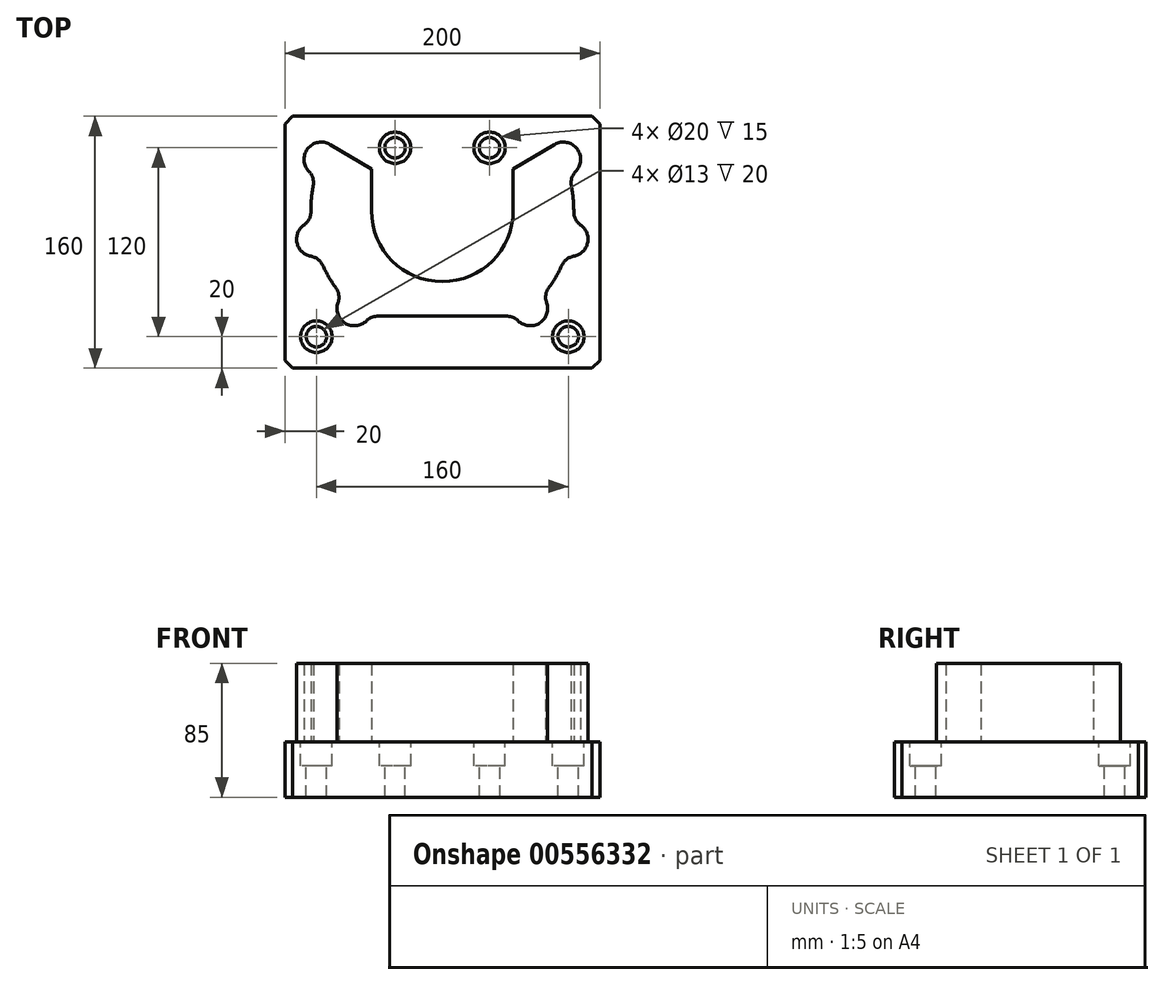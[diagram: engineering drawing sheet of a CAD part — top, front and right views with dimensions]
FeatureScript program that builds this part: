
annotation { "Feature Type Name" : "Feature", "Feature Type Description" : "" }
export const myFeature = defineFeature(function(context is Context, id is Id, definition is map)
    precondition{}
    {
        {
            var Q0;
            Q0=qCreatedBy(makeId("Top.planeOp"),FACE);
            var sketch = newSketch(context, id + "F0", { "sketchPlane" : qUnion([Q0])});
            skLineSegment(sketch, "E0.bottom", {"start": v(100, 80) * mm, "end": v(-100, 80) * mm});
            skLineSegment(sketch, "E0.top", {"start": v(100, -80) * mm, "end": v(-100, -80) * mm});
            skLineSegment(sketch, "E0.left", {"start": v(100, 80) * mm, "end": v(100, -80) * mm});
            skLineSegment(sketch, "E0.right", {"start": v(-100, 80) * mm, "end": v(-100, -80) * mm});
            skPoint(sketch, "E0.middle", {"position": v(0, 0) * mm});
            skSolve(sketch);
        }
        {
            var Q0;
            Q0 = qSketchRegion(id + "F0", true);
            extrude(context, id + "F1", {"entities" : qUnion([Q0]), "depth" : 35 * mm, "offsetDistance" : 25 * mm});
        }
        {
            var Q0;
            Q0=makeQuery(id+"F1.opExtrude","CAP_FACE",FACE,{"disambiguationData":[OSD([sQuery(id+"F0.wireOp",EDGE,"E0.bottom"),sQuery(id+"F0.wireOp",EDGE,"E0.top"),sQuery(id+"F0.wireOp",EDGE,"E0.left"),sQuery(id+"F0.wireOp",EDGE,"E0.right")])],"isStart":false});
            var sketch = newSketch(context, id + "F2", { "sketchPlane" : qUnion([Q0])});
            skArc(sketch, "E1", {"start": v(-81.96, 35.94) * mm, "mid": v(-83.15, 27.64) * mm, "end": v(-83.5, 19.27) * mm});
            skLineSegment(sketch, "E2", {"start": v(-45, 39.1) * mm, "end": v(-76.86, 52.63) * mm});
            skLineSegment(sketch, "E3", {"start": v(0, 20) * mm, "end": v(-81.52, 1.93) * mm});
            skLineSegment(sketch, "E4", {"start": v(0, 20) * mm, "end": v(-55.88, -42.05) * mm});
            skLineSegment(sketch, "E5", {"start": v(0, 20) * mm, "end": v(55.88, -42.05) * mm});
            skLineSegment(sketch, "E6", {"start": v(0, 20) * mm, "end": v(81.52, 1.93) * mm});
            skLineSegment(sketch, "E7", {"start": v(45, 39.1) * mm, "end": v(76.86, 52.63) * mm});
            skLineSegment(sketch, "E8", {"start": v(0, 20) * mm, "end": v(-83.5, 20) * mm});
            skArc(sketch, "E9", {"start": v(-71.26, 62.1) * mm, "mid": v(-85.54, 59.4) * mm, "end": v(-84.68, 44.89) * mm});
            skArc(sketch, "E10", {"start": v(-87.8, 10.97) * mm, "mid": v(-92.26, -0.45) * mm, "end": v(-83.39, -8.91) * mm});
            skArc(sketch, "E11", {"start": v(-66.23, -38.34) * mm, "mid": v(-61.8, -51.32) * mm, "end": v(-48.15, -49.88) * mm});
            skArc(sketch, "E12", {"start": v(48.15, -49.88) * mm, "mid": v(61.8, -51.32) * mm, "end": v(66.23, -38.34) * mm});
            skArc(sketch, "E13", {"start": v(83.39, -8.91) * mm, "mid": v(92.26, -0.45) * mm, "end": v(87.8, 10.97) * mm});
            skArc(sketch, "E14", {"start": v(84.68, 44.89) * mm, "mid": v(85.54, 59.4) * mm, "end": v(71.26, 62.1) * mm});
            skLineSegment(sketch, "E15", {"start": v(-41.13, -47) * mm, "end": v(41.13, -47) * mm});
            skArc(sketch, "E16", {"start": v(-45, 20) * mm, "mid": v(0, -25) * mm, "end": v(45, 20) * mm});
            skLineSegment(sketch, "E17", {"start": v(62.6, 46.58) * mm, "end": v(67.67, 46.58) * mm});
            skLineSegment(sketch, "E18", {"start": v(-71.26, 62.1) * mm, "end": v(-45, 46.58) * mm});
            skLineSegment(sketch, "E19", {"start": v(71.26, 62.1) * mm, "end": v(45, 46.58) * mm});
            skLineSegment(sketch, "E20", {"start": v(45, 46.58) * mm, "end": v(45, 20) * mm});
            skLineSegment(sketch, "E21", {"start": v(-45, 46.58) * mm, "end": v(-45, 20) * mm});
            skArc(sketch, "E22.trimOffspring", {"start": v(83.5, 19.27) * mm, "mid": v(83.15, 27.64) * mm, "end": v(81.96, 35.94) * mm});
            skArc(sketch, "E23.trimOffspring", {"start": v(67.55, -29.08) * mm, "mid": v(72.13, -22.06) * mm, "end": v(75.99, -14.62) * mm});
            skArc(sketch, "E24.trimOffspring", {"start": v(-75.99, -14.62) * mm, "mid": v(-72.13, -22.06) * mm, "end": v(-67.55, -29.08) * mm});
            skArc(sketch, "E25.trimOffspring", {"start": v(66.74, 48.33) * mm, "mid": v(67.16, 47.43) * mm, "end": v(67.67, 46.58) * mm});
            skPoint(sketch, "E26.visualSharp", {"position": v(-80.48, 42.24) * mm});
            skArc(sketch, "E26.filletArc", {"start": v(-81.96, 35.94) * mm, "mid": v(-82.2, 40.75) * mm, "end": v(-84.68, 44.89) * mm});
            skPoint(sketch, "E27.visualSharp", {"position": v(-83.19, 12.8) * mm});
            skArc(sketch, "E27.filletArc", {"start": v(-87.8, 10.97) * mm, "mid": v(-84.62, 14.58) * mm, "end": v(-83.5, 19.27) * mm});
            skPoint(sketch, "E28.visualSharp", {"position": v(-78.44, -8.63) * mm});
            skArc(sketch, "E28.filletArc", {"start": v(-75.99, -14.62) * mm, "mid": v(-78.98, -10.85) * mm, "end": v(-83.39, -8.91) * mm});
            skPoint(sketch, "E29.visualSharp", {"position": v(-63.55, -34.17) * mm});
            skArc(sketch, "E29.filletArc", {"start": v(-66.23, -38.34) * mm, "mid": v(-65.74, -33.54) * mm, "end": v(-67.55, -29.08) * mm});
            skPoint(sketch, "E30.visualSharp", {"position": v(-46.05, -47) * mm});
            skArc(sketch, "E30.filletArc", {"start": v(-41.13, -47) * mm, "mid": v(-44.92, -47.75) * mm, "end": v(-48.15, -49.88) * mm});
            skPoint(sketch, "E31.visualSharp", {"position": v(46.05, -47) * mm});
            skArc(sketch, "E31.filletArc", {"start": v(48.15, -49.88) * mm, "mid": v(44.92, -47.75) * mm, "end": v(41.13, -47) * mm});
            skPoint(sketch, "E32.visualSharp", {"position": v(63.55, -34.17) * mm});
            skArc(sketch, "E32.filletArc", {"start": v(67.55, -29.08) * mm, "mid": v(65.74, -33.54) * mm, "end": v(66.23, -38.34) * mm});
            skPoint(sketch, "E33.visualSharp", {"position": v(78.44, -8.63) * mm});
            skArc(sketch, "E33.filletArc", {"start": v(83.39, -8.91) * mm, "mid": v(78.98, -10.85) * mm, "end": v(75.99, -14.62) * mm});
            skPoint(sketch, "E34.visualSharp", {"position": v(83.19, 12.8) * mm});
            skArc(sketch, "E34.filletArc", {"start": v(83.5, 19.27) * mm, "mid": v(84.62, 14.58) * mm, "end": v(87.8, 10.97) * mm});
            skPoint(sketch, "E35.visualSharp", {"position": v(80.48, 42.24) * mm});
            skArc(sketch, "E35.filletArc", {"start": v(84.68, 44.89) * mm, "mid": v(82.2, 40.75) * mm, "end": v(81.96, 35.94) * mm});
            skLineSegment(sketch, "E36", {"start": v(-100, 20) * mm, "end": v(100, 20) * mm});
            skSolve(sketch);
        }
        {
            var Q0;
            Q0=makeQuery(id+"F2.imprint","IMPRINT",FACE,{"disambiguationData":[TD([[makeQuery(id+"F2.imprint","IMPRINT",EDGE,{"derivedFrom":sQuery(id+"F2.wireOp",EDGE,"E10")}),1.0]])]});
            var Q1;
            Q1=makeQuery(id+"F2.imprint","IMPRINT",FACE,{"disambiguationData":[TD([[makeQuery(id+"F2.imprint","IMPRINT",EDGE,{"derivedFrom":sQuery(id+"F2.wireOp",EDGE,"E9")}),1.0]])]});
            var Q2;
            Q2=makeQuery(id+"F2.imprint","IMPRINT",FACE,{"disambiguationData":[TD([[makeQuery(id+"F2.imprint","IMPRINT",EDGE,{"derivedFrom":sQuery(id+"F2.wireOp",EDGE,"E14")}),1.0]])]});
            var Q3;
            {var subQ0=sQuery(id+"F2.wireOp",EDGE,"E17");Q3=makeQuery(id+"F2.imprint","IMPRINT",FACE,{"disambiguationData":[TD([[makeQuery(id+"F2.imprint","IMPRINT",EDGE,{"derivedFrom":subQ0}),1.0]])]});}
            extrude(context, id + "F3", {"entities" : qUnion([Q0, Q1, Q2, Q3]), "operationType" : NewBodyOperationType.ADD, "depth" : 50 * mm, "offsetDistance" : 25 * mm});
        }
        {
            var Q0;
            Q0=makeQuery(id+"F1.opExtrude","SWEPT_EDGE",EDGE,{"disambiguationData":[OSD([sQuery(id+"F0.wireOp",EDGE,"E0.top"),sQuery(id+"F0.wireOp",EDGE,"E0.left")])]});
            var Q1;
            Q1=makeQuery(id+"F1.opExtrude","SWEPT_EDGE",EDGE,{"disambiguationData":[OSD([sQuery(id+"F0.wireOp",EDGE,"E0.bottom"),sQuery(id+"F0.wireOp",EDGE,"E0.left")])]});
            var Q2;
            Q2=makeQuery(id+"F1.opExtrude","SWEPT_EDGE",EDGE,{"disambiguationData":[OSD([sQuery(id+"F0.wireOp",EDGE,"E0.bottom"),sQuery(id+"F0.wireOp",EDGE,"E0.right")])]});
            var Q3;
            Q3=makeQuery(id+"F1.opExtrude","SWEPT_EDGE",EDGE,{"disambiguationData":[OSD([sQuery(id+"F0.wireOp",EDGE,"E0.top"),sQuery(id+"F0.wireOp",EDGE,"E0.right")])]});
            chamfer(context, id + "F4", {"entities" : qUnion([Q0, Q1, Q2, Q3]), "width" : 5 * mm, "tangentPropagation" : true});
        }
        {
            var Q0;
            Q0=makeQuery(id+"F1.opExtrude","CAP_FACE",FACE,{"disambiguationData":[OSD([sQuery(id+"F0.wireOp",EDGE,"E0.bottom"),sQuery(id+"F0.wireOp",EDGE,"E0.top"),sQuery(id+"F0.wireOp",EDGE,"E0.left"),sQuery(id+"F0.wireOp",EDGE,"E0.right")])],"isStart":false});
            var sketch = newSketch(context, id + "F5", { "sketchPlane" : qUnion([Q0])});
            skLineSegment(sketch, "E37", {"start": v(-100, 20) * mm, "end": v(100, 20) * mm});
            skCircle(sketch, "E38", {"center": v(-80, -60) * mm, "radius": 10 * mm});
            skCircle(sketch, "E39", {"center": v(80, -60) * mm, "radius": 10 * mm});
            skCircle(sketch, "E40", {"center": v(-30, 60) * mm, "radius": 10 * mm});
            skCircle(sketch, "E41", {"center": v(30, 60) * mm, "radius": 10 * mm});
            skSolve(sketch);
        }
        {
            var Q0;
            Q0 = qSketchRegion(id + "F5", true);
            extrude(context, id + "F6", {"entities" : qUnion([Q0]), "operationType" : NewBodyOperationType.REMOVE, "oppositeDirection" : true, "depth" : 15 * mm, "offsetDistance" : 25 * mm});
        }
        {
            var Q0;
            Q0=makeQuery(id+"F6.boolean.opBoolean","COPY",FACE,{"derivedFrom":makeQuery(id+"F6.opExtrude","CAP_FACE",FACE,{"disambiguationData":[OSD([sQuery(id+"F5.wireOp",EDGE,"E39")])],"isStart":false})});
            var sketch = newSketch(context, id + "F7", { "sketchPlane" : qUnion([Q0])});
            skCircle(sketch, "E42.0", {"center": v(-80, -60) * mm, "radius": 10 * mm});
            skCircle(sketch, "E43.0", {"center": v(80, -60) * mm, "radius": 10 * mm});
            skCircle(sketch, "E44.0", {"center": v(30, 60) * mm, "radius": 10 * mm});
            skCircle(sketch, "E45.0", {"center": v(-30, 60) * mm, "radius": 10 * mm});
            skCircle(sketch, "E46", {"center": v(-30, 60) * mm, "radius": 6.5 * mm});
            skCircle(sketch, "E47", {"center": v(30, 60) * mm, "radius": 6.5 * mm});
            skCircle(sketch, "E48", {"center": v(-80, -60) * mm, "radius": 6.5 * mm});
            skCircle(sketch, "E49", {"center": v(80, -60) * mm, "radius": 6.5 * mm});
            skSolve(sketch);
        }
        {
            var Q0;
            Q0=makeQuery(id+"F7.imprint","IMPRINT",FACE,{"disambiguationData":[TD([[makeQuery(id+"F7.imprint","IMPRINT",EDGE,{"derivedFrom":sQuery(id+"F7.wireOp",EDGE,"E46")}),1.0]])]});
            var Q1;
            Q1=makeQuery(id+"F7.imprint","IMPRINT",FACE,{"disambiguationData":[TD([[makeQuery(id+"F7.imprint","IMPRINT",EDGE,{"derivedFrom":sQuery(id+"F7.wireOp",EDGE,"E47")}),1.0]])]});
            var Q2;
            Q2=makeQuery(id+"F7.imprint","IMPRINT",FACE,{"disambiguationData":[TD([[makeQuery(id+"F7.imprint","IMPRINT",EDGE,{"derivedFrom":sQuery(id+"F7.wireOp",EDGE,"E48")}),1.0]])]});
            var Q3;
            Q3=makeQuery(id+"F7.imprint","IMPRINT",FACE,{"disambiguationData":[TD([[makeQuery(id+"F7.imprint","IMPRINT",EDGE,{"derivedFrom":sQuery(id+"F7.wireOp",EDGE,"E49")}),1.0]])]});
            extrude(context, id + "F8", {"entities" : qUnion([Q0, Q1, Q2, Q3]), "operationType" : NewBodyOperationType.REMOVE, "oppositeDirection" : true, "depth" : 20 * mm, "offsetDistance" : 25 * mm});
        }
    });
